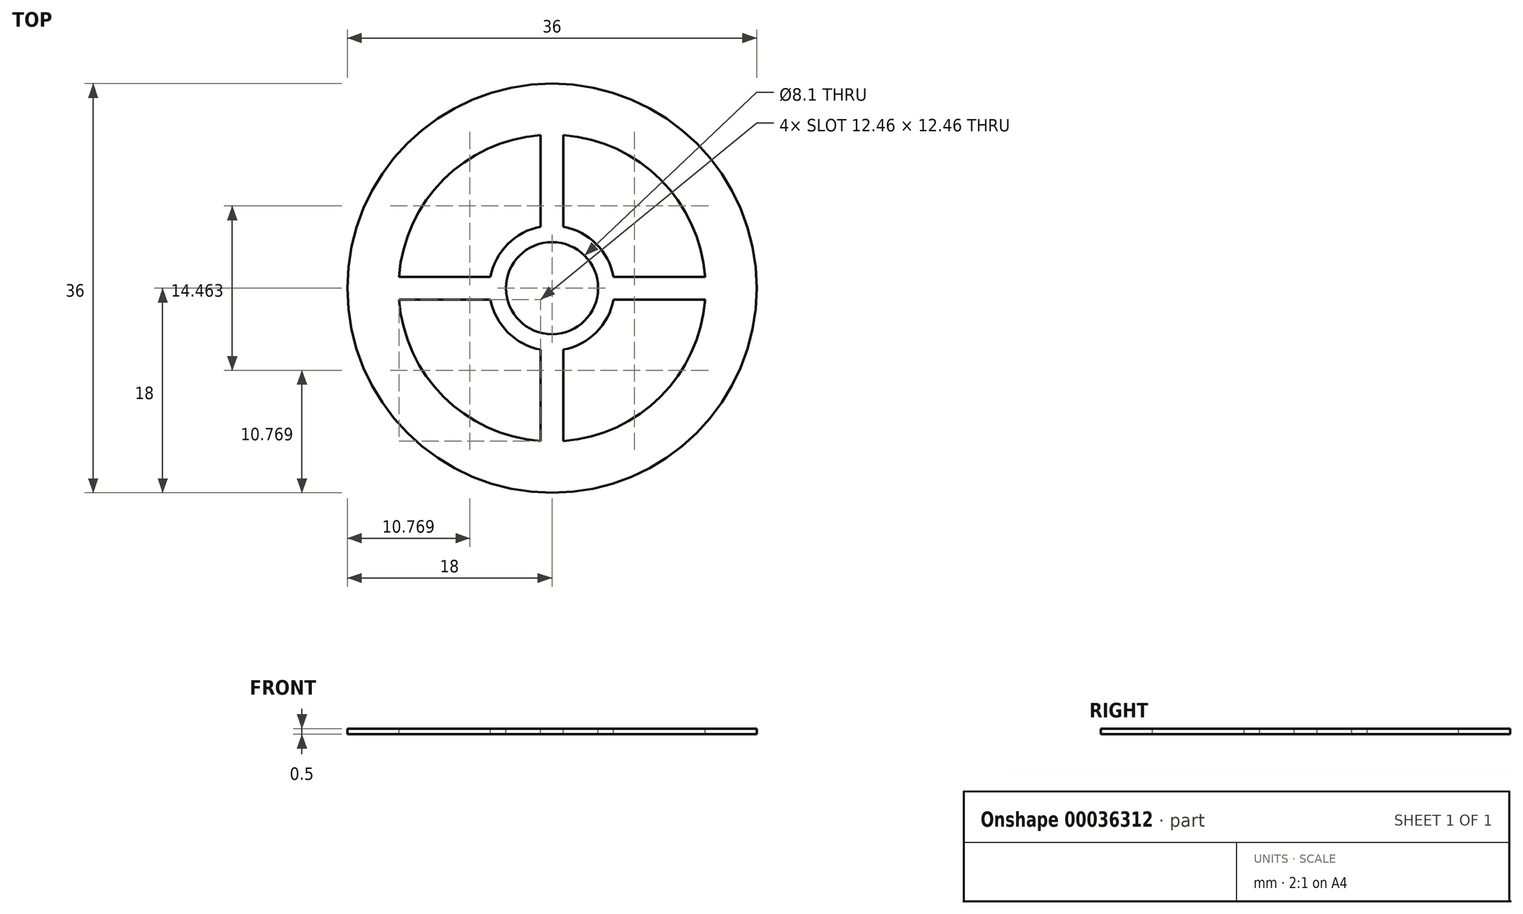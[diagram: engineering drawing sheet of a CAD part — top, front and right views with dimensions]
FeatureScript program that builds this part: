
annotation { "Feature Type Name" : "Feature", "Feature Type Description" : "" }
export const myFeature = defineFeature(function(context is Context, id is Id, definition is map)
    precondition{}
    {
        {
            var Q0;
            Q0=qCreatedBy(makeId("Top.planeOp"),FACE);
            var sketch = newSketch(context, id + "F0", { "sketchPlane" : qUnion([Q0])});
            skCircle(sketch, "E0", {"center": v(0, 0) * mm, "radius": 18 * mm});
            skSolve(sketch);
        }
        {
            var Q0;
            Q0=makeQuery(id+"F0.imprint","IMPRINT",FACE,{"disambiguationData":[TD([[makeQuery(id+"F0.imprint","IMPRINT",EDGE,{"derivedFrom":sQuery(id+"F0.wireOp",EDGE,"E0")}),1.0]])]});
            extrude(context, id + "F1", {"entities" : qUnion([Q0]), "depth" : 0.5 * mm});
        }
        {
            var Q0;
            Q0=makeQuery(id+"F1.opExtrude","CAP_FACE",FACE,{"disambiguationData":[OSD([sQuery(id+"F0.wireOp",EDGE,"E0")])],"isStart":false});
            var sketch = newSketch(context, id + "F2", { "sketchPlane" : qUnion([Q0])});
            skCircle(sketch, "E1", {"center": v(0, 0) * mm, "radius": 4.05 * mm});
            skSolve(sketch);
        }
        {
            var Q0;
            Q0=makeQuery(id+"F2.imprint","IMPRINT",FACE,{"disambiguationData":[TD([[makeQuery(id+"F2.imprint","IMPRINT",EDGE,{"derivedFrom":sQuery(id+"F2.wireOp",EDGE,"E1")}),1.0]])]});
            extrude(context, id + "F3", {"entities" : qUnion([Q0]), "operationType" : NewBodyOperationType.REMOVE, "endBound" : BoundingType.UP_TO_NEXT, "oppositeDirection" : true, "depth" : 25 * mm});
        }
        {
            var Q0;
            Q0=makeQuery(id+"F1.opExtrude","CAP_FACE",FACE,{"disambiguationData":[OSD([sQuery(id+"F0.wireOp",EDGE,"E0")])],"isStart":false});
            var sketch = newSketch(context, id + "F4", { "sketchPlane" : qUnion([Q0])});
            skCircle(sketch, "E2", {"center": v(0, 0) * mm, "radius": 5.5 * mm});
            skLineSegment(sketch, "E3.left", {"start": v(-1, 13.46) * mm, "end": v(-1, 5.4) * mm});
            skLineSegment(sketch, "E3.right", {"start": v(1, 13.46) * mm, "end": v(1, 5.4) * mm});
            skLineSegment(sketch, "E4", {"start": v(0, 13.5) * mm, "end": v(0, 5.5) * mm, "construction": true});
            skLineSegment(sketch, "E5", {"start": v(1, -5.4) * mm, "end": v(1, -13.46) * mm});
            skLineSegment(sketch, "E6", {"start": v(-1, -5.4) * mm, "end": v(-1, -13.46) * mm});
            skLineSegment(sketch, "E7", {"start": v(0, 0) * mm, "end": v(13.5, 0) * mm, "construction": true});
            skLineSegment(sketch, "E8.0", {"start": v(5.4, 1) * mm, "end": v(13.46, 1) * mm});
            skLineSegment(sketch, "E9.0", {"start": v(5.4, -1) * mm, "end": v(13.46, -1) * mm});
            skLineSegment(sketch, "E10", {"start": v(-5.4, -1) * mm, "end": v(-13.46, -1) * mm});
            skLineSegment(sketch, "E11", {"start": v(-5.4, 1) * mm, "end": v(-13.46, 1) * mm});
            skCircle(sketch, "E12", {"center": v(0, 0) * mm, "radius": 13.5 * mm});
            skSolve(sketch);
        }
        {
            var Q0;
            {var subQ2=sQuery(id+"F4.wireOp",EDGE,"E6");Q0=makeQuery(id+"F4.imprint","IMPRINT",FACE,{"disambiguationData":[TD([[makeQuery(id+"F4.imprint","IMPRINT",EDGE,{"derivedFrom":subQ2}),-1.0]])]});}
            var Q1;
            {var subQ2=sQuery(id+"F4.wireOp",EDGE,"E5");Q1=makeQuery(id+"F4.imprint","IMPRINT",FACE,{"disambiguationData":[TD([[makeQuery(id+"F4.imprint","IMPRINT",EDGE,{"derivedFrom":subQ2}),1.0]])]});}
            var Q2;
            {var subQ2=sQuery(id+"F4.wireOp",EDGE,"E3.right");Q2=makeQuery(id+"F4.imprint","IMPRINT",FACE,{"disambiguationData":[TD([[makeQuery(id+"F4.imprint","IMPRINT",EDGE,{"derivedFrom":subQ2}),1.0]])]});}
            var Q3;
            {var subQ2=sQuery(id+"F4.wireOp",EDGE,"E3.left");Q3=makeQuery(id+"F4.imprint","IMPRINT",FACE,{"disambiguationData":[TD([[makeQuery(id+"F4.imprint","IMPRINT",EDGE,{"derivedFrom":subQ2}),-1.0]])]});}
            extrude(context, id + "F5", {"entities" : qUnion([Q0, Q1, Q2, Q3]), "operationType" : NewBodyOperationType.REMOVE, "endBound" : BoundingType.UP_TO_NEXT, "oppositeDirection" : true, "depth" : 25 * mm});
        }
    });
